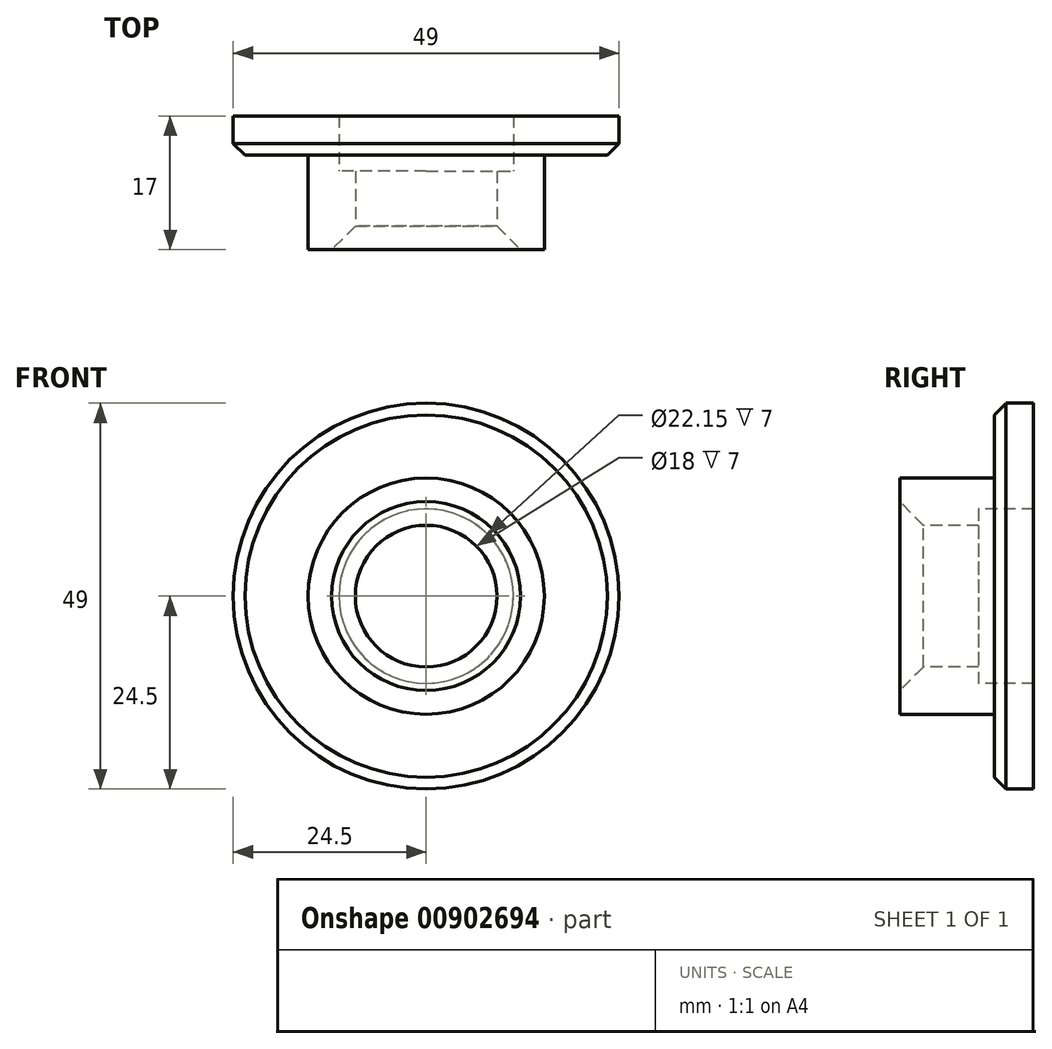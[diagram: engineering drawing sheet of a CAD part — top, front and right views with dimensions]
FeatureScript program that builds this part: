
annotation { "Feature Type Name" : "Feature", "Feature Type Description" : "" }
export const myFeature = defineFeature(function(context is Context, id is Id, definition is map)
    precondition{}
    {
        {
            var Q0;
            Q0=qCreatedBy(makeId("Front.planeOp"),FACE);
            var sketch = newSketch(context, id + "F0", { "sketchPlane" : qUnion([Q0])});
            skCircle(sketch, "E0", {"center": v(0, 0) * mm, "radius": 15 * mm});
            skSolve(sketch);
        }
        {
            var Q0;
            Q0=makeQuery(id+"F0.imprint","IMPRINT",FACE,{"disambiguationData":[TD([[makeQuery(id+"F0.imprint","IMPRINT",EDGE,{"derivedFrom":sQuery(id+"F0.wireOp",EDGE,"E0")}),1.0]])]});
            extrude(context, id + "F1", {"entities" : qUnion([Q0]), "depth" : 7 * mm, "offsetDistance" : 25 * mm, "hasSecondDirection" : true, "secondDirectionOppositeDirection" : true, "secondDirectionDepth" : 5 * mm});
        }
        {
            var Q0;
            Q0=makeQuery(id+"F1.opExtrude","CAP_FACE",FACE,{"disambiguationData":[OSD([sQuery(id+"F0.wireOp",EDGE,"E0")])],"isStart":false});
            var sketch = newSketch(context, id + "F2", { "sketchPlane" : qUnion([Q0])});
            skCircle(sketch, "E1", {"center": v(0, 0) * mm, "radius": 11.08 * mm});
            skSolve(sketch);
        }
        {
            var Q0;
            Q0=makeQuery(id+"F2.imprint","IMPRINT",FACE,{"disambiguationData":[TD([[makeQuery(id+"F2.imprint","IMPRINT",EDGE,{"derivedFrom":sQuery(id+"F2.wireOp",EDGE,"E1")}),1.0]])]});
            extrude(context, id + "F3", {"entities" : qUnion([Q0]), "operationType" : NewBodyOperationType.REMOVE, "endBound" : BoundingType.THROUGH_ALL, "oppositeDirection" : true, "depth" : 8.5 * mm, "offsetDistance" : 25 * mm});
        }
        {
            var Q0;
            Q0=makeQuery(id+"F1.opExtrude","CAP_FACE",FACE,{"disambiguationData":[OSD([sQuery(id+"F0.wireOp",EDGE,"E0")])],"isStart":true});
            var sketch = newSketch(context, id + "F4", { "sketchPlane" : qUnion([Q0])});
            skCircle(sketch, "E2", {"center": v(0, 0) * mm, "radius": 24.5 * mm});
            skCircle(sketch, "E3", {"center": v(0, 0) * mm, "radius": 11.08 * mm});
            skSolve(sketch);
        }
        {
            var Q0;
            Q0 = qSketchRegion(id + "F4", true);
            extrude(context, id + "F5", {"entities" : qUnion([Q0]), "operationType" : NewBodyOperationType.ADD, "depth" : 5 * mm, "offsetDistance" : 25 * mm});
        }
        {
            var Q0;
            Q0=makeQuery(id+"F1.opExtrude","CAP_FACE",FACE,{"disambiguationData":[OSD([sQuery(id+"F0.wireOp",EDGE,"E0")])],"isStart":false});
            var sketch = newSketch(context, id + "F6", { "sketchPlane" : qUnion([Q0])});
            skCircle(sketch, "E4", {"center": v(0, 0) * mm, "radius": 11.08 * mm});
            skCircle(sketch, "E5", {"center": v(0, 0) * mm, "radius": 9 * mm});
            skSolve(sketch);
        }
        {
            var Q0;
            Q0 = qSketchRegion(id + "F6", true);
            var Q1;
            Q1=makeQuery(id+"F5.opExtrude","CAP_FACE",FACE,{"disambiguationData":[OSD([sQuery(id+"F4.wireOp",EDGE,"E2"),sQuery(id+"F4.wireOp",EDGE,"E3")])],"isStart":false});
            extrude(context, id + "F7", {"entities" : qUnion([Q0]), "operationType" : NewBodyOperationType.ADD, "endBound" : BoundingType.UP_TO_SURFACE, "oppositeDirection" : true, "depth" : 5 * mm, "endBoundEntityFace" : qUnion([Q1]), "hasOffset" : true, "offsetDistance" : 7 * mm});
        }
        {
            var Q0;
            Q0=makeQuery(id+"F5.opExtrude","CAP_EDGE",EDGE,{"disambiguationData":[OSD([sQuery(id+"F4.wireOp",EDGE,"E2")])],"isStart":true});
            chamfer(context, id + "F8", {"entities" : qUnion([Q0]), "width" : 1.5 * mm, "tangentPropagation" : true});
        }
        {
            var Q0;
            Q0=makeQuery(id+"F7.opExtrude","CAP_EDGE",EDGE,{"disambiguationData":[OSD([sQuery(id+"F6.wireOp",EDGE,"E5")])],"isStart":true});
            chamfer(context, id + "F9", {"entities" : qUnion([Q0]), "width" : 3 * mm, "tangentPropagation" : true});
        }
    });
